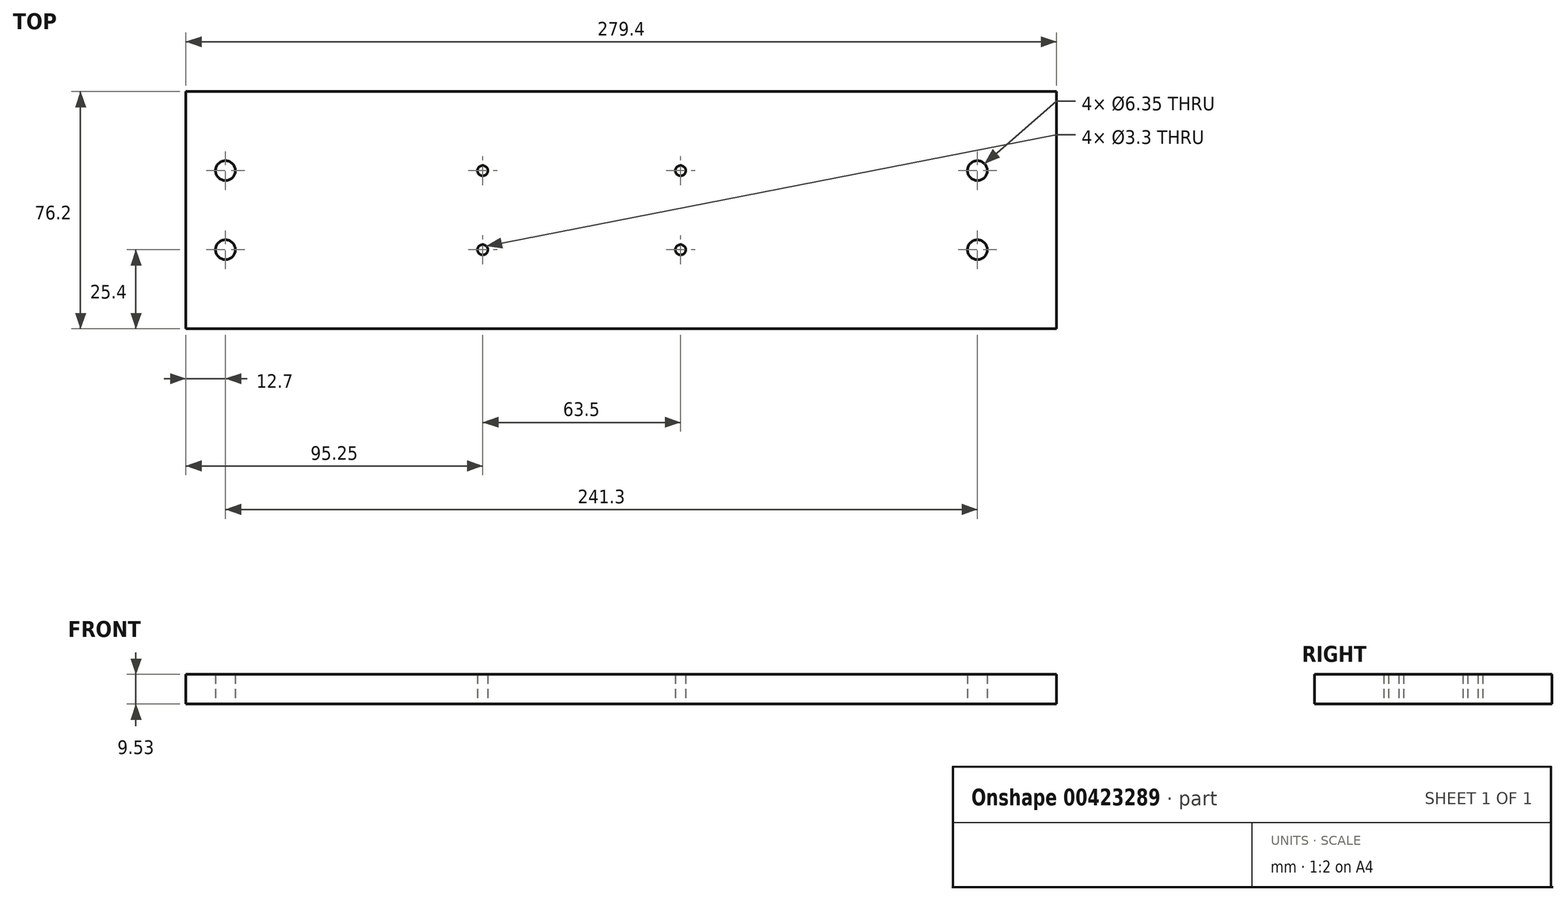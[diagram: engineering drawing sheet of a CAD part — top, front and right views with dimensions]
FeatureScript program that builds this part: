
annotation { "Feature Type Name" : "Feature", "Feature Type Description" : "" }
export const myFeature = defineFeature(function(context is Context, id is Id, definition is map)
    precondition{}
    {
        {
            var Q0;
            Q0=qCreatedBy(makeId("Top.planeOp"),FACE);
            var sketch = newSketch(context, id + "F0", { "sketchPlane" : qUnion([Q0])});
            skLineSegment(sketch, "E0.bottom", {"start": v(-139.7, 38.1) * mm, "end": v(139.7, 38.1) * mm});
            skLineSegment(sketch, "E0.top", {"start": v(-139.7, -38.1) * mm, "end": v(139.7, -38.1) * mm});
            skLineSegment(sketch, "E0.left", {"start": v(-139.7, 38.1) * mm, "end": v(-139.7, -38.1) * mm});
            skLineSegment(sketch, "E0.right", {"start": v(139.7, 38.1) * mm, "end": v(139.7, -38.1) * mm});
            skLineSegment(sketch, "E1.bottom", {"start": v(-127, 12.7) * mm, "end": v(114.3, 12.7) * mm, "construction": true});
            skLineSegment(sketch, "E1.top", {"start": v(-127, -12.7) * mm, "end": v(114.3, -12.7) * mm, "construction": true});
            skLineSegment(sketch, "E1.left", {"start": v(-127, 12.7) * mm, "end": v(-127, -12.7) * mm, "construction": true});
            skLineSegment(sketch, "E1.right", {"start": v(114.3, 12.7) * mm, "end": v(114.3, -12.7) * mm, "construction": true});
            skCircle(sketch, "E2", {"center": v(-127, 12.7) * mm, "radius": 3.17 * mm});
            skCircle(sketch, "E3", {"center": v(-127, -12.7) * mm, "radius": 3.17 * mm});
            skCircle(sketch, "E4", {"center": v(-44.45, 12.7) * mm, "radius": 1.65 * mm});
            skCircle(sketch, "E5", {"center": v(-44.45, -12.7) * mm, "radius": 1.65 * mm});
            skCircle(sketch, "E6", {"center": v(19.05, 12.7) * mm, "radius": 1.65 * mm});
            skCircle(sketch, "E7", {"center": v(19.05, -12.7) * mm, "radius": 1.65 * mm});
            skCircle(sketch, "E8", {"center": v(114.3, 12.7) * mm, "radius": 3.18 * mm});
            skCircle(sketch, "E9", {"center": v(114.3, -12.7) * mm, "radius": 3.18 * mm});
            skSolve(sketch);
        }
        {
            var Q0;
            Q0 = qSketchRegion(id + "F0", true);
            extrude(context, id + "F1", {"entities" : qUnion([Q0]), "depth" : 9.52 * mm});
        }
    });
